# Revit family: 2CKA001032A0490
name_source: partatom
category: Elektroinstallationen
revit_build: Autodesk Revit 2017 (Build: 20160225_1515(x64)
units: mm (PartAtom-declared; Revit-internal decimal feet)

## family parameters
Basisbauteil = Fläche
Beim Laden mit Abzugskörper schneiden = Nein
Bemaßung runder Anschluss = Durchmesser verwenden
Beschriftungsausrichtung beibehalten = Nein
Gemeinsam genutzt = Nein
Raumberechnungspunkt = Nein
Teiletyp = Normal

## types (1)
- 2CKA001032A0490
    BIM = https://media.live.bim.site
    BIMSITE_PRODUCT_ID = 658b21c95d61cb6f7f2337e4dd0635c47c576c68
    Beschreibung = El. Raumtemperaturregler UP, UP-Montagedosen und -Einsätze, Einsätze für Raumtemperaturregler, El. Raumtemperaturregler UP Wechsler, Istwert-Anzeige Mit Temperaturanzeige IST-Wert Automatische Reglerkalibrierung Mit Spreizbefestigung Klasse des Temperaturreglers: 1 Beitrag zur Raumheizungsenergieeffizienz: 1,0%. Nennstrom: 5 A EN 60730-2-9, British Standard EN 60669-2-1
    Datenblatt = https://media.live.bim.site
    GTIN = 4011395078648
    Gerätebreite [mm] = 54
    Gerätehöhe [mm] = 54
    Gerätetiefe [mm] = 23
    Gewicht [kg/m] = 0.12
    Glass = Glass
    HAN = 2CKA001032A0490
    HeinzeBIM = https://www.heinze.de
    Hersteller = Busch-Jaeger
    Ist System = Nein
    Ist Zubehör = Nein
    Produktseite = https://media.live.bim.site
    TYPE = 1097 UTA
    Typname = El. Raumtemperaturregler UP, UP-Montagedosen und -Einsätze, Einsätze für Raumtemperaturregler
    URL = https://www.busch-jaeger.de
    Vorgabe-Ansicht = 1219 mm
    White = White

## geometry (parser evidence)
native form markers: Sweep x3
no freeform markers — native parametric forms only
